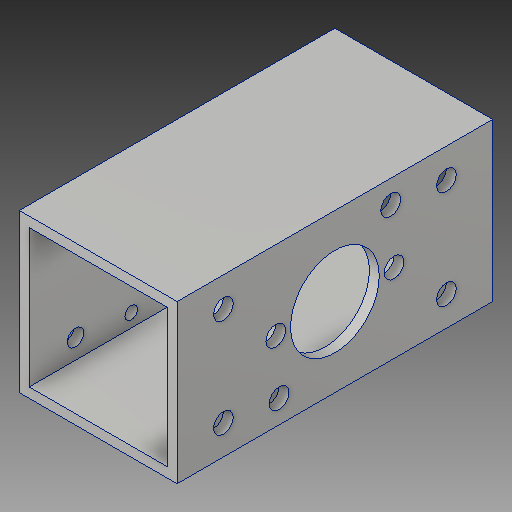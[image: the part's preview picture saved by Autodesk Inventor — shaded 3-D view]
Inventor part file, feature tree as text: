
AUTODESK INVENTOR PART (.ipt)
format: ipt  version: 2019 (Build 230136000, 136)  size: 183,296 bytes
history: native  units: in
note: dims shown in document units (in); Inventor stores cm internally (conversion verified against a paired STEP export)
features: reference x11, extrude x7, sketch x7, other x4
ambient origin geometry x8: Origin, YZ Plane, XZ Plane, XY Plane, X Axis, Y Axis, Z Axis, Center Point
bodies: Solid1 (feature_tree)
feature tree (29):
  extrude  "Extrusion1"  Depth=0.125in
  extrude  "Extrusion7"  Depth=2.0in
  extrude  "Extrusion8"  Depth=1.0in TaperAngle=0.0deg
  extrude  "Extrusion9"  Depth=1.0in TaperAngle=0.0deg
  extrude  "Extrusion10"  Depth=1.0in TaperAngle=0.0deg
  extrude  "Extrusion11"  Depth=1.0in TaperAngle=0.0deg
  extrude  "Extrusion12"  Depth=1.0in TaperAngle=0.0deg
  sketch  "Sketch1"  dims[d0=2.0in d1=0.125in]
  sketch  "Sketch6"  dims[d2=4.0in d3=0.0in d11=2.0in]
  reference  "Reference2"
  sketch  "Sketch7"  dims[d12=0.125in d23=1.0in d24=0.0in]
  sketch  "Sketch8"  dims[d25=1.125in d26=1.0in d27=0.0in]
  reference  "Reference3"
  reference  "Reference4"
  reference  "Reference5"
  reference  "Reference6"
  sketch  "Sketch9"  dims[d28=1.0in d29=0.0in d30=1.0in d31=0.0in]
  reference  "Reference7"
  reference  "Reference8"
  reference  "Reference9"
  reference  "Reference10"
  sketch  "Sketch10"  dims[d32=0.25in d33=1.0in d34=0.0in]
  reference  "Reference11"
  reference  "Reference12"
  sketch  "Sketch11"  dims[d35=0.25in d36=1.0in d37=0.0in]
  parser-record x1  (decoder bookkeeping rows leaked as tree rows — omitted from the tree; the rows remain in map.json)
  other  "Drive Arm.iam"
  other  "Arm 2 inch A:1"
  other  "Arm 2 inch C:1"
note: 1 file-system path scrubbed to <path> (originals preserved in map.json)
